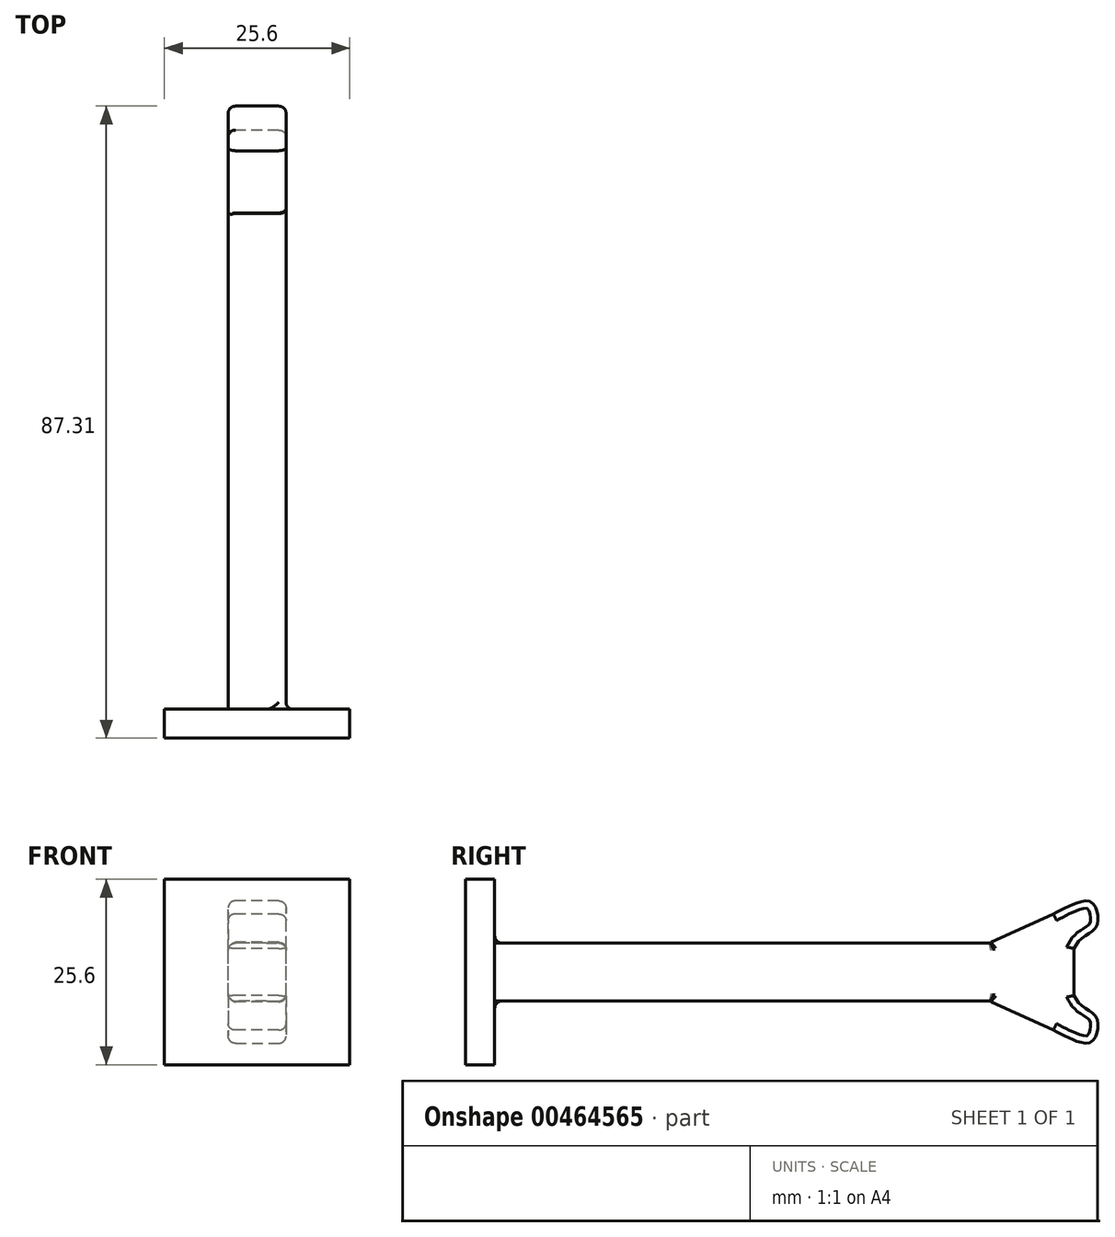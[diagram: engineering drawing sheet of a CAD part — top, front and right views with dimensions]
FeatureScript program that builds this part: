
annotation { "Feature Type Name" : "Feature", "Feature Type Description" : "" }
export const myFeature = defineFeature(function(context is Context, id is Id, definition is map)
    precondition{}
    {
        {
            var Q0;
            Q0=qCreatedBy(makeId("Front.planeOp"),FACE);
            var sketch = newSketch(context, id + "F0", { "sketchPlane" : qUnion([Q0])});
            skLineSegment(sketch, "E0.bottom", {"start": v(12.8, 12.8) * mm, "end": v(-12.8, 12.8) * mm});
            skLineSegment(sketch, "E0.top", {"start": v(12.8, -12.8) * mm, "end": v(-12.8, -12.8) * mm});
            skLineSegment(sketch, "E0.left", {"start": v(12.8, 12.8) * mm, "end": v(12.8, -12.8) * mm});
            skLineSegment(sketch, "E0.right", {"start": v(-12.8, 12.8) * mm, "end": v(-12.8, -12.8) * mm});
            skPoint(sketch, "E0.middle", {"position": v(0, 0) * mm});
            skSolve(sketch);
        }
        {
            var Q0;
            Q0=qCreatedBy(makeId("Front.planeOp"),FACE);
            var sketch = newSketch(context, id + "F1", { "sketchPlane" : qUnion([Q0])});
            skLineSegment(sketch, "E1.bottom", {"start": v(4, -4) * mm, "end": v(-4, -4) * mm});
            skLineSegment(sketch, "E1.top", {"start": v(4, 4) * mm, "end": v(-4, 4) * mm});
            skLineSegment(sketch, "E1.left", {"start": v(4, -4) * mm, "end": v(4, 4) * mm});
            skLineSegment(sketch, "E1.right", {"start": v(-4, -4) * mm, "end": v(-4, 4) * mm});
            skPoint(sketch, "E1.middle", {"position": v(0, 0) * mm});
            skSolve(sketch);
        }
        {
            var Q0;
            Q0 = qSketchRegion(id + "F0", true);
            extrude(context, id + "F2", {"entities" : qUnion([Q0]), "depth" : 4 * mm});
        }
        {
            var Q0;
            Q0 = qSketchRegion(id + "F1", true);
            extrude(context, id + "F3", {"entities" : qUnion([Q0]), "operationType" : NewBodyOperationType.ADD, "oppositeDirection" : true, "depth" : 80 * mm});
        }
        {
            var Q0;
            Q0=qCreatedBy(makeId("Right.planeOp"),FACE);
            var sketch = newSketch(context, id + "F4", { "sketchPlane" : qUnion([Q0])});
            skLineSegment(sketch, "E2", {"start": v(68.56, 4.1) * mm, "end": v(77.14, 8.02) * mm});
            skFitSpline(sketch, "E3", {"points": [v(79.82, 0) * mm, v(80.88, 4.48) * mm, v(83.12, 6.34) * mm, v(82.65, 9.42) * mm, v(80.88, 9.7) * mm, v(77.14, 8.02) * mm], "startDerivative": vector(-7.43, 22.3) * mm, "endDerivative": vector(-17.65, -9.2) * mm});
            skLineSegment(sketch, "E4", {"start": v(68.56, 4.1) * mm, "end": v(65.39, 0) * mm});
            skLineSegment(sketch, "E5.MirrorCS", {"start": v(68.56, -4.1) * mm, "end": v(65.39, 0) * mm});
            skLineSegment(sketch, "E6.MirrorCS", {"start": v(68.56, -4.1) * mm, "end": v(77.14, -8.02) * mm});
            skFitSpline(sketch, "E7.MirrorCS", {"points": [v(79.82, 0) * mm, v(80.88, -4.48) * mm, v(83.12, -6.34) * mm, v(82.65, -9.42) * mm, v(80.88, -9.7) * mm, v(77.14, -8.02) * mm], "startDerivative": vector(-7.43, -22.3) * mm, "endDerivative": vector(-17.65, 9.2) * mm});
            skSolve(sketch);
        }
        {
            var Q0;
            Q0 = qSketchRegion(id + "F4", true);
            extrude(context, id + "F5", {"entities" : qUnion([Q0]), "operationType" : NewBodyOperationType.ADD, "depth" : 4 * mm, "hasSecondDirection" : true, "secondDirectionOppositeDirection" : true, "secondDirectionDepth" : 4 * mm});
        }
        {
            var Q0;
            Q0=makeQuery(id+"F5.boolean.opBoolean","MERGE",FACE,{"derivedFrom":[makeQuery(id+"F3.opExtrude","SWEPT_FACE",FACE,{"disambiguationData":[OSD([sQuery(id+"F1.wireOp",EDGE,"E1.left")])]}),makeQuery(id+"F5.opExtrude","CAP_FACE",FACE,{"disambiguationData":[OSD([sQuery(id+"F4.wireOp",EDGE,"E2"),sQuery(id+"F4.wireOp",EDGE,"E3"),sQuery(id+"F4.wireOp",EDGE,"E4"),sQuery(id+"F4.wireOp",EDGE,"E5.MirrorCS"),sQuery(id+"F4.wireOp",EDGE,"E6.MirrorCS"),sQuery(id+"F4.wireOp",EDGE,"E7.MirrorCS")])],"isStart":false})]});
            var Q1;
            Q1=makeQuery(id+"F5.opExtrude","CAP_EDGE",EDGE,{"disambiguationData":[OSD([sQuery(id+"F4.wireOp",EDGE,"E7.MirrorCS")])],"isStart":true});
            var Q2;
            Q2=makeQuery(id+"F5.opExtrude","CAP_EDGE",EDGE,{"disambiguationData":[OSD([sQuery(id+"F4.wireOp",EDGE,"E3")])],"isStart":true});
            fillet(context, id + "F6", {"entities" : qUnion([Q0, Q1, Q2]), "radius" : 1 * mm, "tangentPropagation" : true, "allowEdgeOverflow" : false});
        }
        {
            var Q0;
            Q0=makeQuery(id+"F3.opExtrude","SWEPT_EDGE",EDGE,{"disambiguationData":[OSD([sQuery(id+"F1.wireOp",EDGE,"E1.top"),sQuery(id+"F1.wireOp",EDGE,"E1.right")])]});
            var Q1;
            Q1=makeQuery(id+"F3.opExtrude","SWEPT_EDGE",EDGE,{"disambiguationData":[OSD([sQuery(id+"F1.wireOp",EDGE,"E1.bottom"),sQuery(id+"F1.wireOp",EDGE,"E1.right")])]});
            var Q2;
            Q2=makeQuery(id+"F3.opExtrude","CAP_EDGE",EDGE,{"disambiguationData":[OSD([sQuery(id+"F1.wireOp",EDGE,"E1.right")])],"isStart":false});
            var Q3;
            Q3=makeQuery(id+"F3.opExtrude","CAP_EDGE",EDGE,{"disambiguationData":[OSD([sQuery(id+"F1.wireOp",EDGE,"E1.right")])],"isStart":true});
            fillet(context, id + "F7", {"entities" : qUnion([Q0, Q1, Q2, Q3]), "radius" : 1 * mm, "tangentPropagation" : true, "allowEdgeOverflow" : false});
        }
    });
